SOLIDWORKS PART (.sldprt)
format: sldprt  version: not decoded by parser v0  size: 394,240 bytes
history: native  units: mm
features: sketch x7, cut_extrude x5, extrude x2, material x1, plane x1 (+13 scaffold rows collapsed)
feature tree (29):
  scaffold x13  (default folders/planes/origin — collapsed)
  material  "ABS"
  sketch  "Sketch1"  dims[D1=1.8415mm D2=3.175mm]
  extrude  "Boss-Extrude1"  Depth=3.175mm
  plane  "Plane1"
  extrude  "Boss-Extrude2"  [1 undecoded]
  sketch  "Sketch1<3>"
  sketch  "Sketch3"  dims[D3=1.5875mm D1=~0.79375mm D2=1.5875mm]
  cut_extrude  "Cut-Extrude1"  [1 undecoded]
  sketch  "Sketch5"  dims[D2=1.5875mm D1=1.5875mm]
  cut_extrude  "Cut-Extrude2"  Depth=3.175mm
  sketch  "Sketch6"  dims[D1=6.604mm D2=12.954mm]
  cut_extrude  "Cut-Extrude3"  Depth=3.175mm
  sketch  "Sketch7"  dims[D2=1.5875mm D3=6.0mm D1=0.0mm]
  cut_extrude  "Cut-Extrude4"  Depth=3.175mm
  sketch  "Sketch8"  dims[c1.D1=15.24mm c2.D1=90.0deg c3.D1=15.24mm c3.D2=~14.665474mm c4.D2=90.0deg c5.D2=15.875mm c5.D3=15.875mm c6.D3=270.0deg]
  cut_extrude  "Cut-Extrude5"  Depth=0.79375mm
decode coverage: 11 of 14 modeling features carry decoded parameters
note: ~ marks probable driven/reference dimensions
note: 2 parameter values undecoded
note: suppression state not decoded; provenance and decode notes live in map.json
